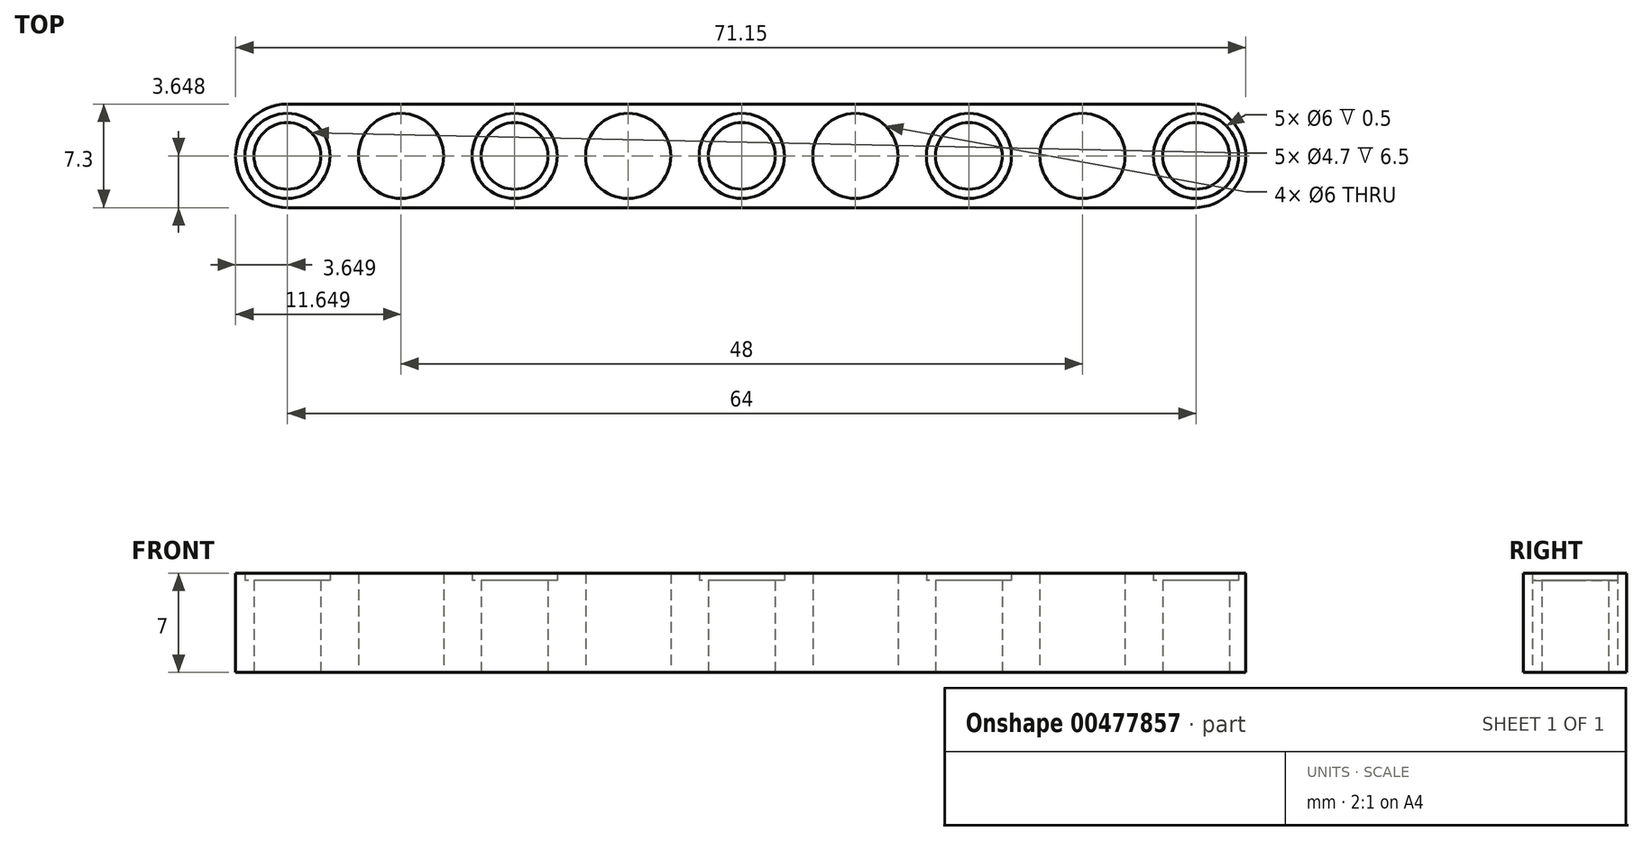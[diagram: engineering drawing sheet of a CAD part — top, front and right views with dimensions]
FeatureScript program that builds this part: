
annotation { "Feature Type Name" : "Feature", "Feature Type Description" : "" }
export const myFeature = defineFeature(function(context is Context, id is Id, definition is map)
    precondition{}
    {
        {
            var Q0;
            Q0=qCreatedBy(makeId("Top.planeOp"),FACE);
            var sketch = newSketch(context, id + "F0", { "sketchPlane" : qUnion([Q0])});
            skLineSegment(sketch, "E0", {"start": v(-58.1, -16.65) * mm, "end": v(5.75, -16.65) * mm});
            skLineSegment(sketch, "E1", {"start": v(9.4, -13) * mm, "end": v(9.4, -13) * mm});
            skLineSegment(sketch, "E2", {"start": v(5.75, -9.35) * mm, "end": v(-58.1, -9.35) * mm});
            skLineSegment(sketch, "E3", {"start": v(-61.75, -13) * mm, "end": v(-61.75, -13) * mm});
            skPoint(sketch, "E4.visualSharp", {"position": v(9.4, -9.35) * mm});
            skArc(sketch, "E4.filletArc", {"start": v(9.4, -13) * mm, "mid": v(8.33, -10.42) * mm, "end": v(5.75, -9.35) * mm});
            skPoint(sketch, "E5.visualSharp", {"position": v(9.4, -16.65) * mm});
            skArc(sketch, "E5.filletArc", {"start": v(5.75, -16.65) * mm, "mid": v(8.33, -15.58) * mm, "end": v(9.4, -13) * mm});
            skPoint(sketch, "E6.visualSharp", {"position": v(-61.75, -9.35) * mm});
            skArc(sketch, "E6.filletArc", {"start": v(-58.1, -9.35) * mm, "mid": v(-60.68, -10.42) * mm, "end": v(-61.75, -13) * mm});
            skPoint(sketch, "E7.visualSharp", {"position": v(-61.75, -16.65) * mm});
            skArc(sketch, "E7.filletArc", {"start": v(-61.75, -13) * mm, "mid": v(-60.68, -15.58) * mm, "end": v(-58.1, -16.65) * mm});
            skCircle(sketch, "E8", {"center": v(5.9, -13) * mm, "radius": 3 * mm});
            skCircle(sketch, "E9", {"center": v(5.9, -13) * mm, "radius": 2.35 * mm});
            skCircle(sketch, "E10.MirrorC", {"center": v(-2.1, -13) * mm, "radius": 3 * mm});
            skCircle(sketch, "E11.MirrorC", {"center": v(-2.1, -13) * mm, "radius": 2.35 * mm});
            skCircle(sketch, "E12.MirrorC", {"center": v(-10.1, -13) * mm, "radius": 3 * mm});
            skCircle(sketch, "E13.MirrorC", {"center": v(-10.1, -13) * mm, "radius": 2.35 * mm});
            skCircle(sketch, "E14.MirrorC", {"center": v(-18.1, -13) * mm, "radius": 3 * mm});
            skCircle(sketch, "E15.MirrorC", {"center": v(-18.1, -13) * mm, "radius": 2.35 * mm});
            skCircle(sketch, "E16.MirrorC", {"center": v(-26.1, -13) * mm, "radius": 3 * mm});
            skCircle(sketch, "E17.MirrorC", {"center": v(-26.1, -13) * mm, "radius": 2.35 * mm});
            skCircle(sketch, "E18.MirrorC", {"center": v(-34.1, -13) * mm, "radius": 3 * mm});
            skCircle(sketch, "E19.MirrorC", {"center": v(-34.1, -13) * mm, "radius": 2.35 * mm});
            skCircle(sketch, "E20.MirrorC", {"center": v(-42.1, -13) * mm, "radius": 3 * mm});
            skCircle(sketch, "E21.MirrorC", {"center": v(-42.1, -13) * mm, "radius": 2.35 * mm});
            skCircle(sketch, "E22.MirrorC", {"center": v(-50.1, -13) * mm, "radius": 3 * mm});
            skCircle(sketch, "E23.MirrorC", {"center": v(-50.1, -13) * mm, "radius": 2.35 * mm});
            skCircle(sketch, "E24.MirrorC", {"center": v(-58.1, -13) * mm, "radius": 3 * mm});
            skCircle(sketch, "E25.MirrorC", {"center": v(-58.1, -13) * mm, "radius": 2.35 * mm});
            skLineSegment(sketch, "E26", {"start": v(9.4, -13) * mm, "end": v(-61.75, -13) * mm, "construction": true});
            skSolve(sketch);
        }
        {
            var Q0;
            Q0=makeQuery(id+"F0.imprint","IMPRINT",FACE,{"disambiguationData":[TD([[makeQuery(id+"F0.imprint","IMPRINT",EDGE,{"derivedFrom":sQuery(id+"F0.wireOp",EDGE,"E0")}),1.0]])]});
            extrude(context, id + "F1", {"entities" : qUnion([Q0]), "depth" : 7.5 * mm});
        }
        {
            var Q0;
            Q0=makeQuery(id+"F0.imprint","IMPRINT",FACE,{"disambiguationData":[TD([[makeQuery(id+"F0.imprint","IMPRINT",EDGE,{"derivedFrom":sQuery(id+"F0.wireOp",EDGE,"E8")}),1.0]])]});
            extrude(context, id + "F2", {"entities" : qUnion([Q0]), "operationType" : NewBodyOperationType.ADD, "depth" : 7 * mm});
        }
        {
            var Q0;
            Q0=makeQuery(id+"F0.imprint","IMPRINT",FACE,{"disambiguationData":[TD([[makeQuery(id+"F0.imprint","IMPRINT",EDGE,{"derivedFrom":sQuery(id+"F0.wireOp",EDGE,"E8")}),1.0]])]});
            extrude(context, id + "F3", {"entities" : qUnion([Q0]), "operationType" : NewBodyOperationType.REMOVE, "depth" : 0.5 * mm});
        }
        {
            var Q0;
            Q0=makeQuery(id+"F0.imprint","IMPRINT",FACE,{"disambiguationData":[TD([[makeQuery(id+"F0.imprint","IMPRINT",EDGE,{"derivedFrom":sQuery(id+"F0.wireOp",EDGE,"E24.MirrorC")}),1.0]])]});
            var Q1;
            Q1=makeQuery(id+"F0.imprint","IMPRINT",FACE,{"disambiguationData":[TD([[makeQuery(id+"F0.imprint","IMPRINT",EDGE,{"derivedFrom":sQuery(id+"F0.wireOp",EDGE,"E22.MirrorC")}),-1.0]])]});
            var Q2;
            Q2=makeQuery(id+"F0.imprint","IMPRINT",FACE,{"disambiguationData":[TD([[makeQuery(id+"F0.imprint","IMPRINT",EDGE,{"derivedFrom":sQuery(id+"F0.wireOp",EDGE,"E20.MirrorC")}),1.0]])]});
            var Q3;
            Q3=makeQuery(id+"F0.imprint","IMPRINT",FACE,{"disambiguationData":[TD([[makeQuery(id+"F0.imprint","IMPRINT",EDGE,{"derivedFrom":sQuery(id+"F0.wireOp",EDGE,"E18.MirrorC")}),-1.0]])]});
            var Q4;
            Q4=makeQuery(id+"F0.imprint","IMPRINT",FACE,{"disambiguationData":[TD([[makeQuery(id+"F0.imprint","IMPRINT",EDGE,{"derivedFrom":sQuery(id+"F0.wireOp",EDGE,"E16.MirrorC")}),1.0]])]});
            var Q5;
            Q5=makeQuery(id+"F0.imprint","IMPRINT",FACE,{"disambiguationData":[TD([[makeQuery(id+"F0.imprint","IMPRINT",EDGE,{"derivedFrom":sQuery(id+"F0.wireOp",EDGE,"E14.MirrorC")}),-1.0]])]});
            var Q6;
            Q6=makeQuery(id+"F0.imprint","IMPRINT",FACE,{"disambiguationData":[TD([[makeQuery(id+"F0.imprint","IMPRINT",EDGE,{"derivedFrom":sQuery(id+"F0.wireOp",EDGE,"E12.MirrorC")}),1.0]])]});
            var Q7;
            Q7=makeQuery(id+"F0.imprint","IMPRINT",FACE,{"disambiguationData":[TD([[makeQuery(id+"F0.imprint","IMPRINT",EDGE,{"derivedFrom":sQuery(id+"F0.wireOp",EDGE,"E10.MirrorC")}),-1.0]])]});
            extrude(context, id + "F4", {"entities" : qUnion([Q0, Q1, Q2, Q3, Q4, Q5, Q6, Q7]), "operationType" : NewBodyOperationType.ADD, "depth" : 7 * mm});
        }
        {
            var Q0;
            Q0=makeQuery(id+"F0.imprint","IMPRINT",FACE,{"disambiguationData":[TD([[makeQuery(id+"F0.imprint","IMPRINT",EDGE,{"derivedFrom":sQuery(id+"F0.wireOp",EDGE,"E24.MirrorC")}),1.0]])]});
            var Q1;
            Q1=makeQuery(id+"F0.imprint","IMPRINT",FACE,{"disambiguationData":[TD([[makeQuery(id+"F0.imprint","IMPRINT",EDGE,{"derivedFrom":sQuery(id+"F0.wireOp",EDGE,"E22.MirrorC")}),-1.0]])]});
            var Q2;
            Q2=makeQuery(id+"F0.imprint","IMPRINT",FACE,{"disambiguationData":[TD([[makeQuery(id+"F0.imprint","IMPRINT",EDGE,{"derivedFrom":sQuery(id+"F0.wireOp",EDGE,"E20.MirrorC")}),1.0]])]});
            var Q3;
            Q3=makeQuery(id+"F0.imprint","IMPRINT",FACE,{"disambiguationData":[TD([[makeQuery(id+"F0.imprint","IMPRINT",EDGE,{"derivedFrom":sQuery(id+"F0.wireOp",EDGE,"E18.MirrorC")}),-1.0]])]});
            var Q4;
            Q4=makeQuery(id+"F0.imprint","IMPRINT",FACE,{"disambiguationData":[TD([[makeQuery(id+"F0.imprint","IMPRINT",EDGE,{"derivedFrom":sQuery(id+"F0.wireOp",EDGE,"E17.MirrorC")}),1.0]])]});
            var Q5;
            Q5=makeQuery(id+"F0.imprint","IMPRINT",FACE,{"disambiguationData":[TD([[makeQuery(id+"F0.imprint","IMPRINT",EDGE,{"derivedFrom":sQuery(id+"F0.wireOp",EDGE,"E14.MirrorC")}),-1.0]])]});
            var Q6;
            Q6=makeQuery(id+"F0.imprint","IMPRINT",FACE,{"disambiguationData":[TD([[makeQuery(id+"F0.imprint","IMPRINT",EDGE,{"derivedFrom":sQuery(id+"F0.wireOp",EDGE,"E12.MirrorC")}),1.0]])]});
            var Q7;
            Q7=makeQuery(id+"F0.imprint","IMPRINT",FACE,{"disambiguationData":[TD([[makeQuery(id+"F0.imprint","IMPRINT",EDGE,{"derivedFrom":sQuery(id+"F0.wireOp",EDGE,"E10.MirrorC")}),-1.0]])]});
            var Q8;
            Q8=makeQuery(id+"F0.imprint","IMPRINT",FACE,{"disambiguationData":[TD([[makeQuery(id+"F0.imprint","IMPRINT",EDGE,{"derivedFrom":sQuery(id+"F0.wireOp",EDGE,"E16.MirrorC")}),1.0]])]});
            extrude(context, id + "F5", {"entities" : qUnion([Q0, Q1, Q2, Q3, Q4, Q5, Q6, Q7, Q8]), "operationType" : NewBodyOperationType.REMOVE, "depth" : 0.5 * mm});
        }
    });
